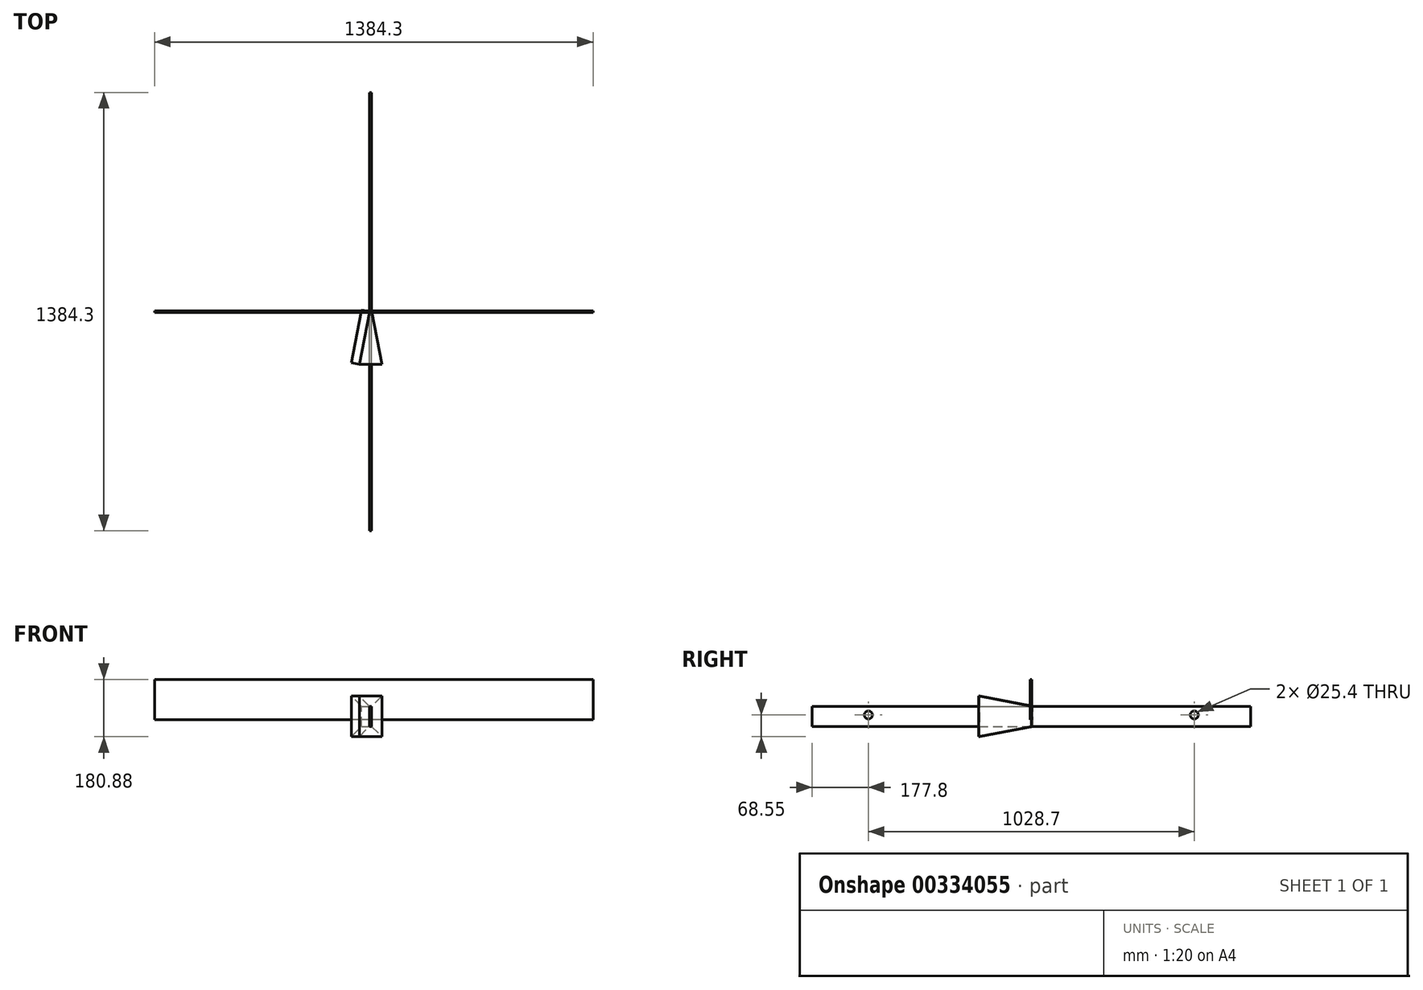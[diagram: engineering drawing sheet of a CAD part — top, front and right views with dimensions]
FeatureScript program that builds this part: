
annotation { "Feature Type Name" : "Feature", "Feature Type Description" : "" }
export const myFeature = defineFeature(function(context is Context, id is Id, definition is map)
    precondition{}
    {
        {
            var Q0;
            Q0=qCreatedBy(makeId("Front.planeOp"),FACE);
            var sketch = newSketch(context, id + "F0", { "sketchPlane" : qUnion([Q0])});
            skLineSegment(sketch, "E0.bottom", {"start": v(-13.42, 10.27) * mm, "end": v(-7.07, 10.27) * mm});
            skLineSegment(sketch, "E0.top", {"start": v(-13.42, -53.23) * mm, "end": v(-7.07, -53.23) * mm});
            skLineSegment(sketch, "E0.left", {"start": v(-13.42, 10.27) * mm, "end": v(-13.42, -53.23) * mm});
            skLineSegment(sketch, "E0.right", {"start": v(-7.07, 10.27) * mm, "end": v(-7.07, -53.23) * mm});
            skSolve(sketch);
        }
        {
            var Q0;
            Q0=makeQuery(id+"F0.imprint","IMPRINT",FACE,{"disambiguationData":[TD([[makeQuery(id+"F0.imprint","IMPRINT",EDGE,{"derivedFrom":sQuery(id+"F0.wireOp",EDGE,"E0.bottom")}),-1.0]])]});
            extrude(context, id + "F1", {"entities" : qUnion([Q0]), "endBound" : BoundingType.SYMMETRIC, "depth" : 1384.3 * mm});
        }
        {
            var Q0;
            Q0=makeQuery(id+"F1.opExtrude","SWEPT_FACE",FACE,{"disambiguationData":[OSD([sQuery(id+"F0.wireOp",EDGE,"E0.right")])]});
            var sketch = newSketch(context, id + "F2", { "sketchPlane" : qUnion([Q0])});
            skPoint(sketch, "E1", {"position": v(-514.35, -17.08) * mm});
            skPoint(sketch, "E2", {"position": v(514.35, -17.08) * mm});
            skSolve(sketch);
        }
        {
            var Q0;
            Q0=sQuery(id+"F2.wireOp",VERTEX,"E1");
            var Q1;
            Q1=sQuery(id+"F2.wireOp",VERTEX,"E2");
            var Q2;
            Q2=makeQuery(id+"F1.opExtrude","SWEPT_BODY",BODY,{"disambiguationData":[OSD([sQuery(id+"F0.wireOp",EDGE,"E0.bottom"),sQuery(id+"F0.wireOp",EDGE,"E0.top"),sQuery(id+"F0.wireOp",EDGE,"E0.left"),sQuery(id+"F0.wireOp",EDGE,"E0.right")])]});
            hole(context, id + "F3", {"style" : HoleStyle.SIMPLE, "endStyle" : HoleEndStyle.THROUGH, "holeDiameter" : 25.4 * mm, "tappedDepth" : 12.7 * mm, "tapClearance" : 3, "locations" : qUnion([Q0, Q1]), "scope" : qUnion([Q2])});
        }
        {
            var Q0;
            Q0 = qSketchRegion(id + "F0", true);
            extrude(context, id + "F4", {"entities" : qUnion([Q0]), "depth" : 166.7 * mm, "hasDraft" : true, "draftAngle" : 11 * degree});
        }
        {
            var Q0;
            Q0=makeQuery(id+"F4.opExtrude","SWEPT_FACE",FACE,{"disambiguationData":[OSD([sQuery(id+"F0.wireOp",EDGE,"E0.left")])]});
            extrude(context, id + "F5", {"entities" : qUnion([Q0]), "depth" : 25.4 * mm});
        }
        {
            var Q0;
            Q0=qCreatedBy(makeId("Right.planeOp"),FACE);
            var sketch = newSketch(context, id + "F6", { "sketchPlane" : qUnion([Q0])});
            skLineSegment(sketch, "E3.bottom", {"start": v(-3.18, 95.25) * mm, "end": v(1.59, 95.25) * mm});
            skLineSegment(sketch, "E3.top", {"start": v(-3.17, -31.75) * mm, "end": v(1.59, -31.75) * mm});
            skLineSegment(sketch, "E3.left", {"start": v(-3.17, 95.25) * mm, "end": v(-3.17, -31.75) * mm});
            skLineSegment(sketch, "E3.right", {"start": v(1.59, 95.25) * mm, "end": v(1.59, -31.75) * mm});
            skSolve(sketch);
        }
        {
            var Q0;
            Q0 = qSketchRegion(id + "F6", true);
            extrude(context, id + "F7", {"entities" : qUnion([Q0]), "endBound" : BoundingType.SYMMETRIC, "depth" : 1384.3 * mm});
        }
    });
